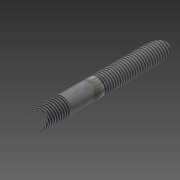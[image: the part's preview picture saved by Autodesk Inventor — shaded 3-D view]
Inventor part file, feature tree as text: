
AUTODESK INVENTOR PART (.ipt)
format: ipt  version: 2015 (Build 190159000, 159)  size: 93,184 bytes
history: native  units: mm
features: thread x2, other x1, extrude x1, sketch x1
ambient origin geometry x8: Origin, YZ Plane, XZ Plane, XY Plane, X Axis, Y Axis, Z Axis, Center Point
bodies: Body1 (feature_tree)
feature tree (5):
  other  "Bryła1"
  extrude  "Wyciągnięcie proste1"  Depth=12.0mm
  thread  "Gwint1"
  thread  "Gwint2"
  sketch  "Szkic1"
